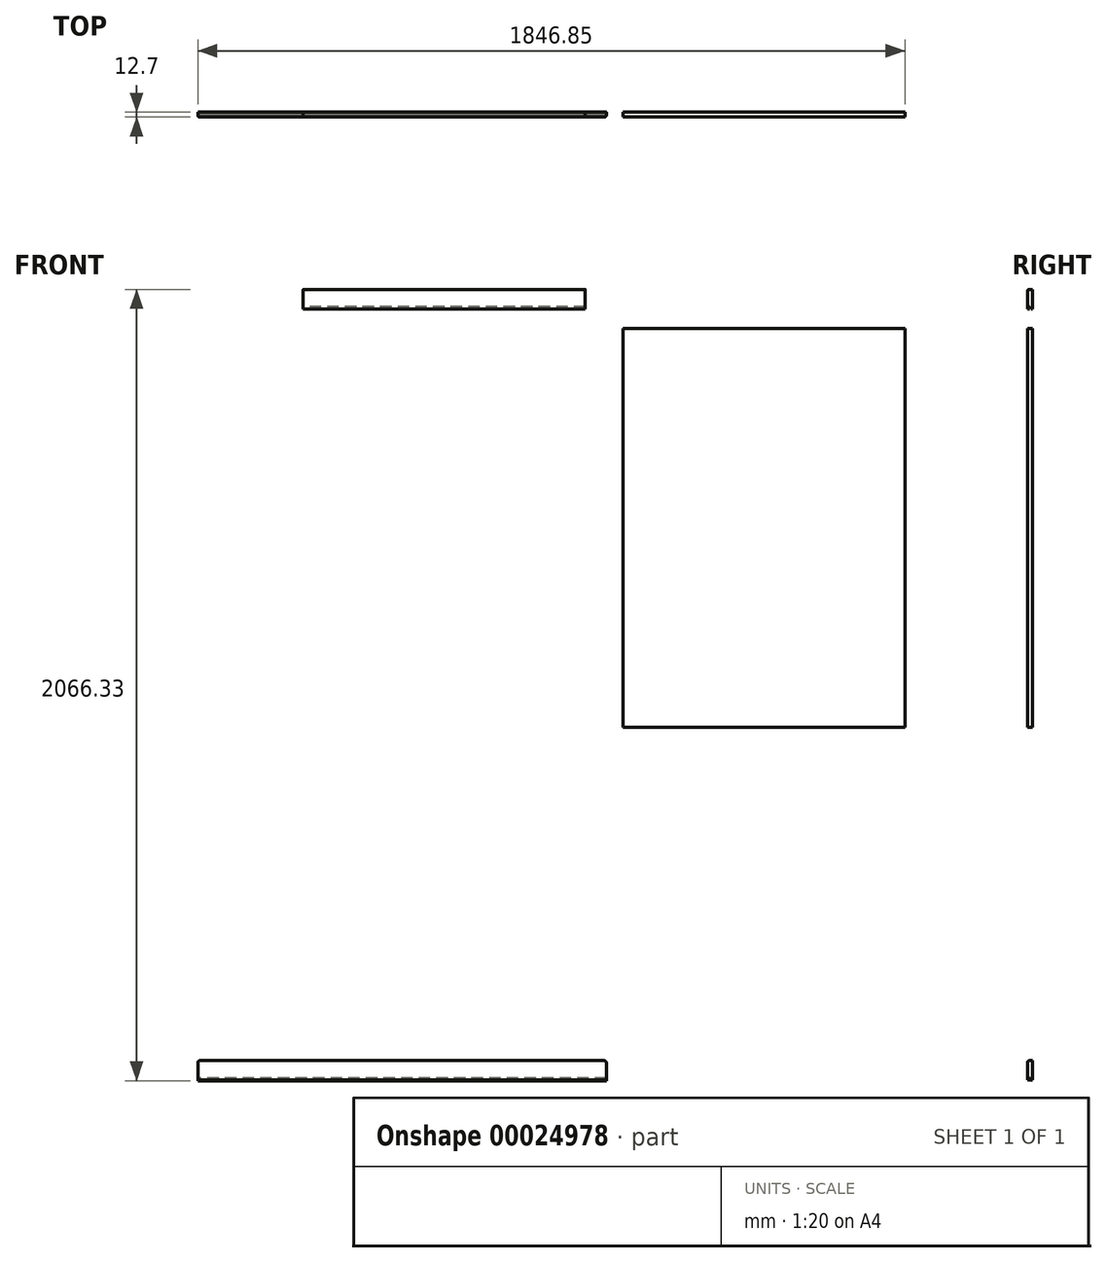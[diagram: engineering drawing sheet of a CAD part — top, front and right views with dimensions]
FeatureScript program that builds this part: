
annotation { "Feature Type Name" : "Feature", "Feature Type Description" : "" }
export const myFeature = defineFeature(function(context is Context, id is Id, definition is map)
    precondition{}
    {
        {
            var Q0;
            Q0=qCreatedBy(makeId("Front.planeOp"),FACE);
            var sketch = newSketch(context, id + "F0", { "sketchPlane" : qUnion([Q0])});
            skLineSegment(sketch, "E0.bottom", {"start": v(-181.13, 768.94) * mm, "end": v(555.47, 768.94) * mm});
            skLineSegment(sketch, "E0.top", {"start": v(-181.13, -272.46) * mm, "end": v(555.47, -272.46) * mm});
            skLineSegment(sketch, "E0.left", {"start": v(-181.13, 768.94) * mm, "end": v(-181.13, -272.46) * mm});
            skLineSegment(sketch, "E0.right", {"start": v(555.47, 768.94) * mm, "end": v(555.47, -272.46) * mm});
            skLineSegment(sketch, "E1.bottom", {"start": v(-1015.97, 871.38) * mm, "end": v(-279.37, 871.38) * mm});
            skLineSegment(sketch, "E1.top", {"start": v(-1015.97, 820.58) * mm, "end": v(-279.37, 820.58) * mm});
            skLineSegment(sketch, "E1.left", {"start": v(-1015.97, 871.38) * mm, "end": v(-1015.97, 820.58) * mm});
            skLineSegment(sketch, "E1.right", {"start": v(-279.37, 871.38) * mm, "end": v(-279.37, 820.58) * mm});
            skLineSegment(sketch, "E2.bottom", {"start": v(-1291.38, -1142.56) * mm, "end": v(-224.58, -1142.56) * mm});
            skLineSegment(sketch, "E2.top", {"start": v(-1291.38, -1193.36) * mm, "end": v(-224.58, -1193.36) * mm});
            skLineSegment(sketch, "E2.left", {"start": v(-1291.38, -1142.56) * mm, "end": v(-1291.38, -1193.36) * mm});
            skLineSegment(sketch, "E2.right", {"start": v(-224.58, -1142.56) * mm, "end": v(-224.58, -1193.36) * mm});
            skSolve(sketch);
        }
        {
            var Q0;
            Q0=makeQuery(id+"F0.imprint","IMPRINT",FACE,{"disambiguationData":[TD([[makeQuery(id+"F0.imprint","IMPRINT",EDGE,{"derivedFrom":sQuery(id+"F0.wireOp",EDGE,"E1.bottom")}),-1.0]])]});
            var Q1;
            Q1=makeQuery(id+"F0.imprint","IMPRINT",FACE,{"disambiguationData":[TD([[makeQuery(id+"F0.imprint","IMPRINT",EDGE,{"derivedFrom":sQuery(id+"F0.wireOp",EDGE,"E0.bottom")}),-1.0]])]});
            var Q2;
            Q2=makeQuery(id+"F0.imprint","IMPRINT",FACE,{"disambiguationData":[TD([[makeQuery(id+"F0.imprint","IMPRINT",EDGE,{"derivedFrom":sQuery(id+"F0.wireOp",EDGE,"E2.bottom")}),-1.0]])]});
            extrude(context, id + "F1", {"entities" : qUnion([Q0, Q1, Q2]), "depth" : 12.7 * mm});
        }
        {
            var Q0;
            Q0=makeQuery(id+"F1.opExtrude","SWEPT_FACE",FACE,{"disambiguationData":[OSD([sQuery(id+"F0.wireOp",EDGE,"E2.left")])]});
            var sketch = newSketch(context, id + "F2", { "sketchPlane" : qUnion([Q0])});
            skLineSegment(sketch, "E3.bottom", {"start": v(-25.26, -1198.78) * mm, "end": v(-22.08, -1198.78) * mm});
            skLineSegment(sketch, "E3.top", {"start": v(-25.26, -1192.43) * mm, "end": v(-22.08, -1192.43) * mm});
            skLineSegment(sketch, "E3.left", {"start": v(-25.26, -1198.78) * mm, "end": v(-25.26, -1192.43) * mm});
            skLineSegment(sketch, "E3.right", {"start": v(-22.08, -1198.78) * mm, "end": v(-22.08, -1192.43) * mm});
            skSolve(sketch);
        }
        {
            var Q0;
            Q0 = qSketchRegion(id + "F2", true);
            extrude(context, id + "F3", {"entities" : qUnion([Q0]), "oppositeDirection" : true, "depth" : 1066.8 * mm});
        }
        {
            var Q0;
            Q0=makeQuery(id+"F3.opExtrude","SWEPT_BODY",BODY,{"disambiguationData":[OSD([sQuery(id+"F2.wireOp",EDGE,"E3.bottom"),sQuery(id+"F2.wireOp",EDGE,"E3.top"),sQuery(id+"F2.wireOp",EDGE,"E3.left"),sQuery(id+"F2.wireOp",EDGE,"E3.right")])]});
            var Q1;
            Q1=makeQuery(id+"F3.opExtrude","SWEPT_EDGE",EDGE,{"disambiguationData":[OSD([sQuery(id+"F2.wireOp",EDGE,"E3.bottom"),sQuery(id+"F2.wireOp",EDGE,"E3.left")])]});
            transform(context, id + "F4", {"entities" : qUnion([Q0]), "transformType" : TransformType.ROTATION, "transformAxis" : qUnion([Q1]), "angle" : 45 * degree, "oppositeDirection" : true, "makeCopy" : false});
        }
        {
            var Q0;
            Q0=makeQuery(id+"F1.opExtrude","SWEPT_FACE",FACE,{"disambiguationData":[OSD([sQuery(id+"F0.wireOp",EDGE,"E2.left")])]});
            var sketch = newSketch(context, id + "F5", { "sketchPlane" : qUnion([Q0])});
            skLineSegment(sketch, "E4.bottom", {"start": v(1.68, -1193.36) * mm, "end": v(4.86, -1193.36) * mm});
            skLineSegment(sketch, "E4.top", {"start": v(1.68, -1187.01) * mm, "end": v(4.86, -1187.01) * mm});
            skLineSegment(sketch, "E4.left", {"start": v(1.68, -1193.36) * mm, "end": v(1.68, -1187.01) * mm});
            skLineSegment(sketch, "E4.right", {"start": v(4.86, -1193.36) * mm, "end": v(4.86, -1187.01) * mm});
            skSolve(sketch);
        }
        {
            var Q0;
            Q0 = qSketchRegion(id + "F5", true);
            extrude(context, id + "F6", {"entities" : qUnion([Q0]), "oppositeDirection" : true, "depth" : 1066.8 * mm});
        }
        {
            var Q0;
            Q0=makeQuery(id+"F6.opExtrude","SWEPT_BODY",BODY,{"disambiguationData":[OSD([sQuery(id+"F5.wireOp",EDGE,"E4.bottom"),sQuery(id+"F5.wireOp",EDGE,"E4.top"),sQuery(id+"F5.wireOp",EDGE,"E4.left"),sQuery(id+"F5.wireOp",EDGE,"E4.right")])]});
            var Q1;
            Q1=makeQuery(id+"F6.opExtrude","SWEPT_EDGE",EDGE,{"disambiguationData":[OSD([sQuery(id+"F0.wireOp",EDGE,"E2.top"),sQuery(id+"F0.wireOp",EDGE,"E2.left"),sQuery(id+"F5.wireOp",EDGE,"E4.bottom"),sQuery(id+"F5.wireOp",EDGE,"E4.left")])]});
            transform(context, id + "F7", {"entities" : qUnion([Q0]), "transformType" : TransformType.ROTATION, "transformAxis" : qUnion([Q1]), "angle" : 30 * degree, "oppositeDirection" : true, "makeCopy" : false});
        }
        {
            var Q0;
            Q0=makeQuery(id+"F3.opExtrude","SWEPT_BODY",BODY,{"disambiguationData":[OSD([sQuery(id+"F2.wireOp",EDGE,"E3.bottom"),sQuery(id+"F2.wireOp",EDGE,"E3.top"),sQuery(id+"F2.wireOp",EDGE,"E3.left"),sQuery(id+"F2.wireOp",EDGE,"E3.right")])]});
            deleteBodies(context, id + "F8", {"entities" : qUnion([Q0])});
        }
        {
            var Q0;
            Q0=makeQuery(id+"F6.opExtrude","SWEPT_BODY",BODY,{"disambiguationData":[OSD([sQuery(id+"F5.wireOp",EDGE,"E4.bottom"),sQuery(id+"F5.wireOp",EDGE,"E4.top"),sQuery(id+"F5.wireOp",EDGE,"E4.left"),sQuery(id+"F5.wireOp",EDGE,"E4.right")])]});
            var Q1;
            Q1=makeQuery(id+"F1.opExtrude","SWEPT_BODY",BODY,{"disambiguationData":[OSD([sQuery(id+"F0.wireOp",EDGE,"E2.bottom"),sQuery(id+"F0.wireOp",EDGE,"E2.top"),sQuery(id+"F0.wireOp",EDGE,"E2.left"),sQuery(id+"F0.wireOp",EDGE,"E2.right")])]});
            booleanBodies(context, id + "F9", {"operationType" : BooleanOperationType.SUBTRACTION, "tools" : qUnion([Q0]), "targets" : qUnion([Q1]), "keepTools" : true});
        }
        {
            var Q0;
            Q0=makeQuery(id+"F1.opExtrude","SWEPT_FACE",FACE,{"disambiguationData":[OSD([sQuery(id+"F0.wireOp",EDGE,"E1.left")])]});
            var sketch = newSketch(context, id + "F10", { "sketchPlane" : qUnion([Q0])});
            skLineSegment(sketch, "E5.bottom", {"start": v(3.18, 820.58) * mm, "end": v(6.35, 820.58) * mm});
            skLineSegment(sketch, "E5.top", {"start": v(3.18, 826.93) * mm, "end": v(6.35, 826.93) * mm});
            skLineSegment(sketch, "E5.left", {"start": v(3.18, 820.58) * mm, "end": v(3.18, 826.93) * mm});
            skLineSegment(sketch, "E5.right", {"start": v(6.35, 820.58) * mm, "end": v(6.35, 826.93) * mm});
            skSolve(sketch);
        }
        {
            var Q0;
            Q0=makeQuery(id+"F10.imprint","IMPRINT",FACE,{"disambiguationData":[TD([[makeQuery(id+"F10.imprint","IMPRINT",EDGE,{"derivedFrom":sQuery(id+"F10.wireOp",EDGE,"E5.bottom")}),-1.0]])]});
            extrude(context, id + "F11", {"entities" : qUnion([Q0]), "oppositeDirection" : true, "depth" : 2540 * mm});
        }
        {
            var Q0;
            Q0=makeQuery(id+"F11.opExtrude","SWEPT_BODY",BODY,{"disambiguationData":[OSD([sQuery(id+"F10.wireOp",EDGE,"E5.bottom"),sQuery(id+"F10.wireOp",EDGE,"E5.top"),sQuery(id+"F10.wireOp",EDGE,"E5.left"),sQuery(id+"F10.wireOp",EDGE,"E5.right")])]});
            var Q1;
            Q1=makeQuery(id+"F11.opExtrude","SWEPT_EDGE",EDGE,{"disambiguationData":[OSD([sQuery(id+"F0.wireOp",EDGE,"E1.top"),sQuery(id+"F0.wireOp",EDGE,"E1.left"),sQuery(id+"F10.wireOp",EDGE,"E5.bottom"),sQuery(id+"F10.wireOp",EDGE,"E5.left")])]});
            transform(context, id + "F12", {"entities" : qUnion([Q0]), "transformType" : TransformType.ROTATION, "transformAxis" : qUnion([Q1]), "angle" : 30 * degree, "oppositeDirection" : true, "makeCopy" : false});
        }
        {
            var Q0;
            Q0=makeQuery(id+"F11.opExtrude","SWEPT_BODY",BODY,{"disambiguationData":[OSD([sQuery(id+"F10.wireOp",EDGE,"E5.bottom"),sQuery(id+"F10.wireOp",EDGE,"E5.top"),sQuery(id+"F10.wireOp",EDGE,"E5.left"),sQuery(id+"F10.wireOp",EDGE,"E5.right")])]});
            var Q1;
            Q1=makeQuery(id+"F1.opExtrude","SWEPT_BODY",BODY,{"disambiguationData":[OSD([sQuery(id+"F0.wireOp",EDGE,"E1.bottom"),sQuery(id+"F0.wireOp",EDGE,"E1.top"),sQuery(id+"F0.wireOp",EDGE,"E1.left"),sQuery(id+"F0.wireOp",EDGE,"E1.right")])]});
            booleanBodies(context, id + "F13", {"operationType" : BooleanOperationType.SUBTRACTION, "tools" : qUnion([Q0]), "targets" : qUnion([Q1])});
        }
        {
            var Q0;
            Q0=makeQuery(id+"F1.opExtrude","CAP_EDGE",EDGE,{"disambiguationData":[OSD([sQuery(id+"F0.wireOp",EDGE,"E1.bottom")])],"isStart":false});
            fillet(context, id + "F14", {"entities" : qUnion([Q0]), "radius" : 5.08 * mm, "tangentPropagation" : true, "allowEdgeOverflow" : false});
        }
        {
            var Q0;
            Q0=makeQuery(id+"F1.opExtrude","CAP_EDGE",EDGE,{"disambiguationData":[OSD([sQuery(id+"F0.wireOp",EDGE,"E2.bottom")])],"isStart":false});
            fillet(context, id + "F15", {"entities" : qUnion([Q0]), "radius" : 5.08 * mm, "tangentPropagation" : true, "allowEdgeOverflow" : false});
        }
        {
            var Q0;
            Q0=makeQuery(id+"F1.opExtrude","SWEPT_EDGE",EDGE,{"disambiguationData":[OSD([sQuery(id+"F0.wireOp",EDGE,"E2.bottom"),sQuery(id+"F0.wireOp",EDGE,"E2.right")])]});
            var Q1;
            Q1=makeQuery(id+"F1.opExtrude","SWEPT_EDGE",EDGE,{"disambiguationData":[OSD([sQuery(id+"F0.wireOp",EDGE,"E2.bottom"),sQuery(id+"F0.wireOp",EDGE,"E2.left")])]});
            fillet(context, id + "F16", {"entities" : qUnion([Q0, Q1]), "radius" : 5.08 * mm, "tangentPropagation" : true, "allowEdgeOverflow" : false});
        }
    });
